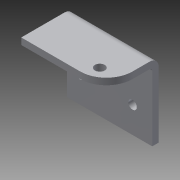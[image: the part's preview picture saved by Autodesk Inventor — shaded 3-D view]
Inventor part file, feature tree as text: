
AUTODESK INVENTOR PART (.ipt)
format: ipt  version: 2014 (Build 180170000, 170)  size: 122,880 bytes
history: native  units: in
note: dims shown in document units (in); Inventor stores cm internally (conversion verified against a paired STEP export)
features: sheet_metal_op x4, sketch x3, other x3
ambient origin geometry x8: Origin, YZ Plane, XZ Plane, XY Plane, X Axis, Y Axis, Z Axis, Center Point
bodies: Solid1 (feature_tree)
feature tree (10):
  sheet_metal_op  "Face1"
  sheet_metal_op  "Flange1"
  sketch  "Sketch1"  dims[d0=1.625in]
  other  "Plate1"
  sketch  "Sketch2"  dims[d1=1.25in]
  other  "Plate2"
  sheet_metal_op  "Bend1"
  sheet_metal_op  "Corner1"
  sketch  "Sketch4"  dims[d2=0.163in d3=0.25in d4=0.7874in d6=1.0in d7=0.3937in d9=1.0in d11=0.125in d12=0.125in d13=0.0625in d14=0.25in d15=0.125in d16=1.0in d17=90.0deg d18=0.05in d19=0.5in d20=0.125in d21=0.125in d22=0.5in d28=0.187in d29=0.25in d30=0.375in d31=0.125in d32=0.0in d34=0.5in]
  other  "Cut2"
